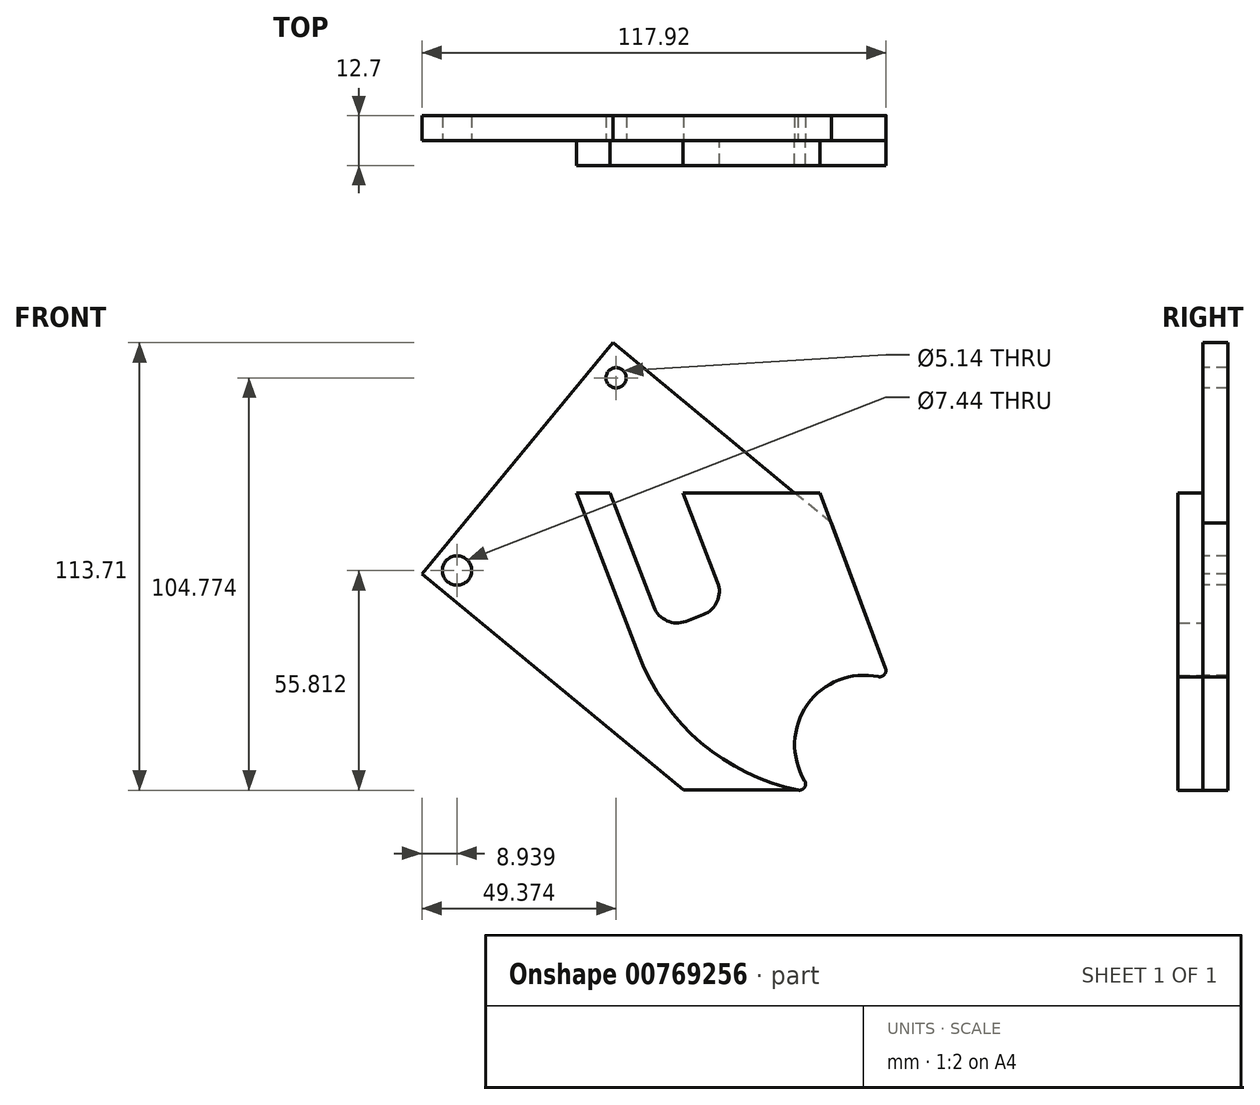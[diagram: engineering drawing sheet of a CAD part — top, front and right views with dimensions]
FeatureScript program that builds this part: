
annotation { "Feature Type Name" : "Feature", "Feature Type Description" : "" }
export const myFeature = defineFeature(function(context is Context, id is Id, definition is map)
    precondition{}
    {
        {
            var Q0;
            Q0=qCreatedBy(makeId("Front.planeOp"),FACE);
            var sketch = newSketch(context, id + "F0", { "sketchPlane" : qUnion([Q0])});
            skLineSegment(sketch, "E0", {"start": v(0, 0) * mm, "end": v(8.5, 0) * mm});
            skLineSegment(sketch, "E1", {"start": v(61.91, 0) * mm, "end": v(78.55, -44.6) * mm});
            skLineSegment(sketch, "E2", {"start": v(79.66, -47.6) * mm, "end": v(60.32, -76.2) * mm, "construction": true});
            skLineSegment(sketch, "E3", {"start": v(15.88, -41.28) * mm, "end": v(0, 0) * mm});
            skPoint(sketch, "E4", {"position": v(15.88, -41.28) * mm});
            skLineSegment(sketch, "E5", {"start": v(0, 0) * mm, "end": v(0, -37.29) * mm, "construction": true});
            skArc(sketch, "E6", {"start": v(15.88, -41.28) * mm, "mid": v(31.72, -63.58) * mm, "end": v(56.32, -75.53) * mm});
            skArc(sketch, "E7", {"start": v(76.73, -46.72) * mm, "mid": v(58.7, -53.8) * mm, "end": v(58, -73.16) * mm});
            skPoint(sketch, "E8.visualSharp", {"position": v(60.32, -76.2) * mm});
            skArc(sketch, "E8.filletArc", {"start": v(56.32, -75.53) * mm, "mid": v(57.94, -74.9) * mm, "end": v(58, -73.16) * mm});
            skPoint(sketch, "E9.visualSharp", {"position": v(79.66, -47.6) * mm});
            skArc(sketch, "E9.filletArc", {"start": v(76.73, -46.72) * mm, "mid": v(78.26, -46.2) * mm, "end": v(78.55, -44.6) * mm});
            skLineSegment(sketch, "E10", {"start": v(8.5, 0) * mm, "end": v(19.66, -29) * mm});
            skLineSegment(sketch, "E11", {"start": v(27.86, -32.65) * mm, "end": v(32.23, -30.96) * mm});
            skLineSegment(sketch, "E12", {"start": v(35.88, -22.76) * mm, "end": v(27.13, 0) * mm});
            skLineSegment(sketch, "E13.trimOffspring", {"start": v(27.13, 0) * mm, "end": v(61.91, 0) * mm});
            skPoint(sketch, "E14.visualSharp", {"position": v(21.94, -34.93) * mm});
            skArc(sketch, "E14.filletArc", {"start": v(19.66, -29) * mm, "mid": v(23, -32.52) * mm, "end": v(27.86, -32.65) * mm});
            skPoint(sketch, "E15.visualSharp", {"position": v(38.16, -28.69) * mm});
            skArc(sketch, "E15.filletArc", {"start": v(32.23, -30.96) * mm, "mid": v(35.76, -27.62) * mm, "end": v(35.88, -22.76) * mm});
            skSolve(sketch);
        }
        {
            var Q0;
            Q0 = qSketchRegion(id + "F0", true);
            extrude(context, id + "F1", {"entities" : qUnion([Q0]), "depth" : 6.35 * mm, "offsetDistance" : 25.4 * mm});
        }
        {
            var Q0;
            Q0=makeQuery(id+"F1.opExtrude","CAP_FACE",FACE,{"disambiguationData":[OSD([sQuery(id+"F0.wireOp",EDGE,"E0"),sQuery(id+"F0.wireOp",EDGE,"E1"),sQuery(id+"F0.wireOp",EDGE,"E3"),sQuery(id+"F0.wireOp",EDGE,"E6"),sQuery(id+"F0.wireOp",EDGE,"E7"),sQuery(id+"F0.wireOp",EDGE,"E8.filletArc"),sQuery(id+"F0.wireOp",EDGE,"E9.filletArc"),sQuery(id+"F0.wireOp",EDGE,"E10"),sQuery(id+"F0.wireOp",EDGE,"E11"),sQuery(id+"F0.wireOp",EDGE,"E12"),sQuery(id+"F0.wireOp",EDGE,"E13.trimOffspring"),sQuery(id+"F0.wireOp",EDGE,"E14.filletArc"),sQuery(id+"F0.wireOp",EDGE,"E15.filletArc")])],"isStart":true});
            var sketch = newSketch(context, id + "F2", { "sketchPlane" : qUnion([Q0])});
            skArc(sketch, "E16.0", {"start": v(-76.73, -46.72) * mm, "mid": v(-58.7, -53.8) * mm, "end": v(-58, -73.16) * mm});
            skArc(sketch, "E16.1", {"start": v(-76.73, -46.72) * mm, "mid": v(-78.26, -46.2) * mm, "end": v(-78.55, -44.6) * mm});
            skArc(sketch, "E16.2", {"start": v(-56.32, -75.53) * mm, "mid": v(-57.94, -74.9) * mm, "end": v(-58, -73.16) * mm});
            skPoint(sketch, "E16.3", {"position": v(-78.26, -46.2) * mm});
            skLineSegment(sketch, "E17", {"start": v(-64.8, -7.72) * mm, "end": v(-9.25, 38.14) * mm});
            skLineSegment(sketch, "E18", {"start": v(-9.25, 38.14) * mm, "end": v(39.27, -20.61) * mm});
            skLineSegment(sketch, "E19", {"start": v(39.27, -20.61) * mm, "end": v(-27.24, -75.53) * mm});
            skLineSegment(sketch, "E20", {"start": v(-78.24, -117.65) * mm, "end": v(-126.76, -58.9) * mm, "construction": true});
            skLineSegment(sketch, "E21", {"start": v(-73.12, -64.02) * mm, "end": v(-102.5, -88.28) * mm, "construction": true});
            skPoint(sketch, "E22", {"position": v(-102.5, -88.28) * mm});
            skLineSegment(sketch, "E23", {"start": v(-78.55, -44.6) * mm, "end": v(-64.8, -7.72) * mm});
            skLineSegment(sketch, "E24", {"start": v(-27.24, -75.53) * mm, "end": v(-56.32, -75.53) * mm});
            skPoint(sketch, "E25", {"position": v(-10.1, 29.2) * mm});
            skPoint(sketch, "E26", {"position": v(30.33, -19.76) * mm});
            skCircle(sketch, "E27", {"center": v(-10.1, 29.2) * mm, "radius": 2.57 * mm});
            skCircle(sketch, "E28", {"center": v(30.33, -19.76) * mm, "radius": 3.72 * mm});
            skSolve(sketch);
        }
        {
            var Q0;
            Q0 = qSketchRegion(id + "F2", true);
            extrude(context, id + "F3", {"entities" : qUnion([Q0]), "depth" : 6.35 * mm, "offsetDistance" : 25.4 * mm});
        }
    });
